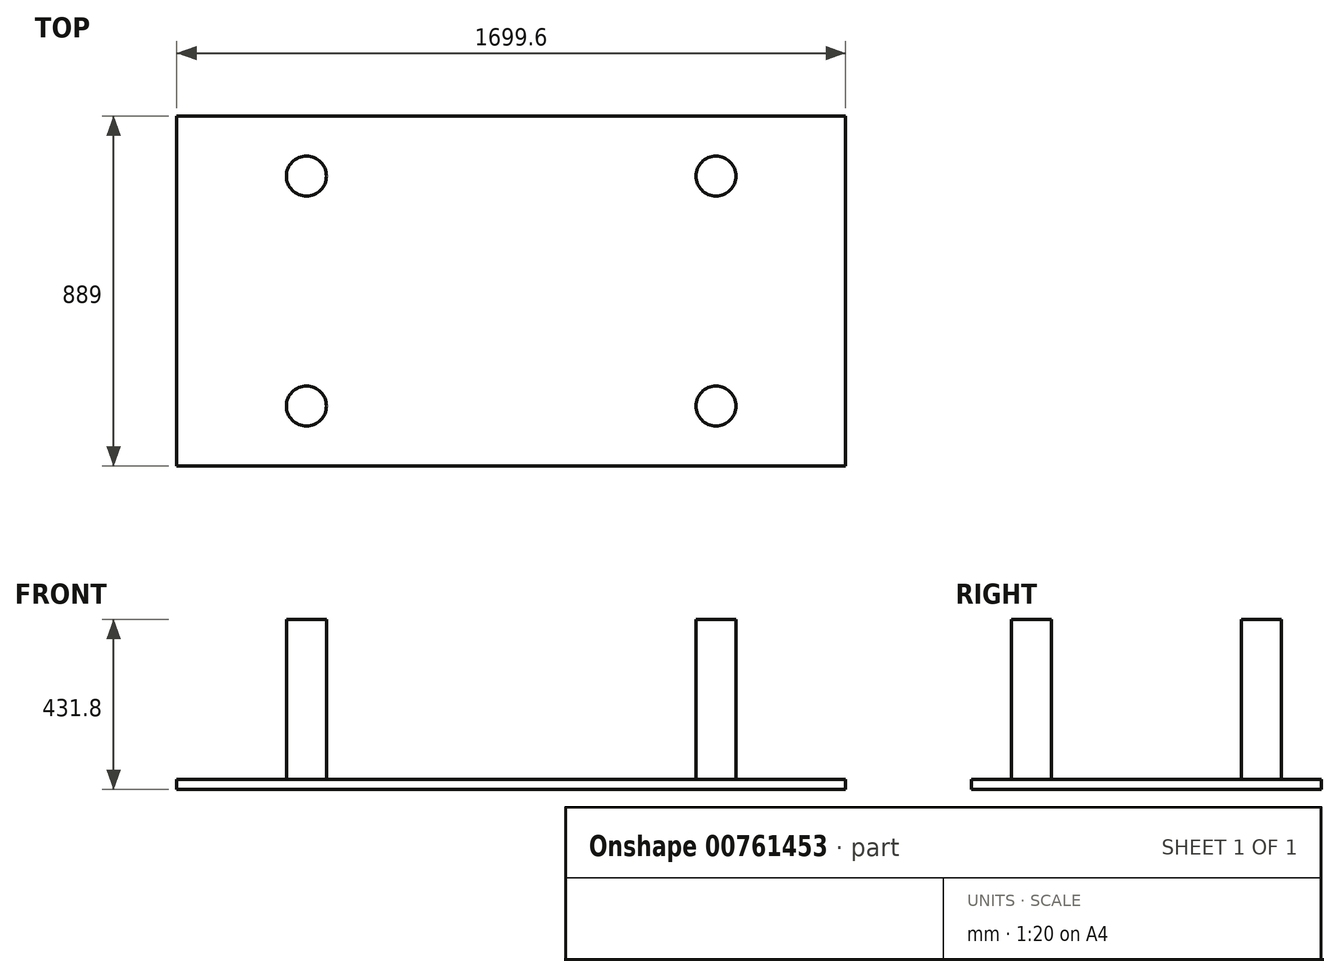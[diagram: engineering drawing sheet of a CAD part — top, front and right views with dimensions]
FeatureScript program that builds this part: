
annotation { "Feature Type Name" : "Feature", "Feature Type Description" : "" }
export const myFeature = defineFeature(function(context is Context, id is Id, definition is map)
    precondition{}
    {
        {
            var Q0;
            Q0=qCreatedBy(makeId("Top.planeOp"),FACE);
            var sketch = newSketch(context, id + "F0", { "sketchPlane" : qUnion([Q0])});
            skLineSegment(sketch, "E0.bottom", {"start": v(-190.5, 381) * mm, "end": v(190.5, 381) * mm});
            skLineSegment(sketch, "E0.top", {"start": v(-190.5, -381) * mm, "end": v(190.5, -381) * mm});
            skLineSegment(sketch, "E0.left", {"start": v(-190.5, 381) * mm, "end": v(-190.5, -381) * mm});
            skLineSegment(sketch, "E0.right", {"start": v(190.5, 381) * mm, "end": v(190.5, -381) * mm});
            skPoint(sketch, "E0.middle", {"position": v(0, 0) * mm});
            skLineSegment(sketch, "E1.bottom", {"start": v(-12.7, 381) * mm, "end": v(12.7, 381) * mm});
            skLineSegment(sketch, "E1.top", {"start": v(-12.7, -381) * mm, "end": v(12.7, -381) * mm});
            skLineSegment(sketch, "E1.left", {"start": v(-12.7, 381) * mm, "end": v(-12.7, -381) * mm});
            skLineSegment(sketch, "E1.right", {"start": v(12.7, 381) * mm, "end": v(12.7, -381) * mm});
            skLineSegment(sketch, "E2", {"start": v(-12.7, 254) * mm, "end": v(12.7, 254) * mm});
            skLineSegment(sketch, "E3", {"start": v(-12.7, 127) * mm, "end": v(12.7, 127) * mm});
            skLineSegment(sketch, "E4", {"start": v(-12.7, 0) * mm, "end": v(12.7, 0) * mm});
            skLineSegment(sketch, "E5", {"start": v(-12.7, -127) * mm, "end": v(12.7, -127) * mm});
            skLineSegment(sketch, "E6", {"start": v(-12.7, -254) * mm, "end": v(12.7, -254) * mm});
            skLineSegment(sketch, "E7.bottom", {"start": v(190.5, 381) * mm, "end": v(-190.5, 381) * mm});
            skLineSegment(sketch, "E7.top", {"start": v(190.5, 508) * mm, "end": v(-190.5, 508) * mm});
            skLineSegment(sketch, "E7.left", {"start": v(190.5, 381) * mm, "end": v(190.5, 508) * mm});
            skLineSegment(sketch, "E7.right", {"start": v(-190.5, 381) * mm, "end": v(-190.5, 508) * mm});
            skLineSegment(sketch, "E8.bottom", {"start": v(849.8, 508) * mm, "end": v(-849.8, 508) * mm});
            skLineSegment(sketch, "E9", {"start": v(-849.8, -381) * mm, "end": v(-190.5, -381) * mm});
            skLineSegment(sketch, "E10", {"start": v(190.5, -381) * mm, "end": v(849.8, -381) * mm});
            skLineSegment(sketch, "E11", {"start": v(849.8, 508) * mm, "end": v(849.8, -381) * mm});
            skLineSegment(sketch, "E12", {"start": v(-849.8, 508) * mm, "end": v(-849.8, -381) * mm});
            skLineSegment(sketch, "E13", {"start": v(-190.5, 508) * mm, "end": v(-849.8, 508) * mm});
            skLineSegment(sketch, "E14", {"start": v(190.5, 508) * mm, "end": v(849.8, 508) * mm});
            skCircle(sketch, "E15", {"center": v(-520.15, 355.6) * mm, "radius": 50.8 * mm});
            skPoint(sketch, "E15.centerSnap0", {"position": v(-520.15, 508) * mm});
            skCircle(sketch, "E16", {"center": v(520.15, 355.6) * mm, "radius": 50.8 * mm});
            skPoint(sketch, "E16.centerSnap0", {"position": v(520.15, 508) * mm});
            skCircle(sketch, "E17", {"center": v(520.15, -228.6) * mm, "radius": 50.8 * mm});
            skCircle(sketch, "E18", {"center": v(-520.15, -228.6) * mm, "radius": 50.8 * mm});
            skSolve(sketch);
        }
        {
            var Q0;
            {var subQ0=sQuery(id+"F0.wireOp",EDGE,"E7.left");Q0=makeQuery(id+"F0.imprint","IMPRINT",FACE,{"disambiguationData":[TD([[makeQuery(id+"F0.imprint","IMPRINT",EDGE,{"derivedFrom":subQ0}),1.0]])]});}
            var Q1;
            {var subQ4=sQuery(id+"F0.wireOp",EDGE,"E0.right");Q1=makeQuery(id+"F0.imprint","IMPRINT",FACE,{"disambiguationData":[TD([[makeQuery(id+"F0.imprint","IMPRINT",EDGE,{"derivedFrom":subQ4}),-1.0]])]});}
            var Q2;
            Q2=makeQuery(id+"F0.imprint","IMPRINT",FACE,{"disambiguationData":[TD([[makeQuery(id+"F0.imprint","IMPRINT",EDGE,{"derivedFrom":sQuery(id+"F0.wireOp",EDGE,"E0.right")}),1.0]])]});
            var Q3;
            Q3=makeQuery(id+"F0.imprint","IMPRINT",FACE,{"disambiguationData":[TD([[makeQuery(id+"F0.imprint","IMPRINT",EDGE,{"derivedFrom":sQuery(id+"F0.wireOp",EDGE,"E16")}),1.0]])]});
            var Q4;
            Q4=makeQuery(id+"F0.imprint","IMPRINT",FACE,{"disambiguationData":[TD([[makeQuery(id+"F0.imprint","IMPRINT",EDGE,{"derivedFrom":sQuery(id+"F0.wireOp",EDGE,"E17")}),1.0]])]});
            var Q5;
            {var subQ4=sQuery(id+"F0.wireOp",EDGE,"E0.left");Q5=makeQuery(id+"F0.imprint","IMPRINT",FACE,{"disambiguationData":[TD([[makeQuery(id+"F0.imprint","IMPRINT",EDGE,{"derivedFrom":subQ4}),1.0]])]});}
            var Q6;
            Q6=makeQuery(id+"F0.imprint","IMPRINT",FACE,{"disambiguationData":[TD([[makeQuery(id+"F0.imprint","IMPRINT",EDGE,{"derivedFrom":sQuery(id+"F0.wireOp",EDGE,"E0.left")}),-1.0]])]});
            var Q7;
            Q7=makeQuery(id+"F0.imprint","IMPRINT",FACE,{"disambiguationData":[TD([[makeQuery(id+"F0.imprint","IMPRINT",EDGE,{"derivedFrom":sQuery(id+"F0.wireOp",EDGE,"E15")}),1.0]])]});
            var Q8;
            Q8=makeQuery(id+"F0.imprint","IMPRINT",FACE,{"disambiguationData":[TD([[makeQuery(id+"F0.imprint","IMPRINT",EDGE,{"derivedFrom":sQuery(id+"F0.wireOp",EDGE,"E18")}),1.0]])]});
            var Q9;
            {var subQ3=sQuery(id+"F0.wireOp",EDGE,"E6");Q9=makeQuery(id+"F0.imprint","IMPRINT",FACE,{"disambiguationData":[TD([[makeQuery(id+"F0.imprint","IMPRINT",EDGE,{"derivedFrom":subQ3}),-1.0]])]});}
            var Q10;
            {var subQ0=sQuery(id+"F0.wireOp",EDGE,"E5");Q10=makeQuery(id+"F0.imprint","IMPRINT",FACE,{"disambiguationData":[TD([[makeQuery(id+"F0.imprint","IMPRINT",EDGE,{"derivedFrom":subQ0}),-1.0]])]});}
            var Q11;
            {var subQ0=sQuery(id+"F0.wireOp",EDGE,"E4");Q11=makeQuery(id+"F0.imprint","IMPRINT",FACE,{"disambiguationData":[TD([[makeQuery(id+"F0.imprint","IMPRINT",EDGE,{"derivedFrom":subQ0}),-1.0]])]});}
            var Q12;
            {var subQ0=sQuery(id+"F0.wireOp",EDGE,"E3");Q12=makeQuery(id+"F0.imprint","IMPRINT",FACE,{"disambiguationData":[TD([[makeQuery(id+"F0.imprint","IMPRINT",EDGE,{"derivedFrom":subQ0}),-1.0]])]});}
            var Q13;
            {var subQ3=sQuery(id+"F0.wireOp",EDGE,"E2");Q13=makeQuery(id+"F0.imprint","IMPRINT",FACE,{"disambiguationData":[TD([[makeQuery(id+"F0.imprint","IMPRINT",EDGE,{"derivedFrom":subQ3}),1.0]])]});}
            var Q14;
            {var subQ0=sQuery(id+"F0.wireOp",EDGE,"E2");Q14=makeQuery(id+"F0.imprint","IMPRINT",FACE,{"disambiguationData":[TD([[makeQuery(id+"F0.imprint","IMPRINT",EDGE,{"derivedFrom":subQ0}),-1.0]])]});}
            extrude(context, id + "F1", {"entities" : qUnion([Q0, Q1, Q2, Q3, Q4, Q5, Q6, Q7, Q8, Q9, Q10, Q11, Q12, Q13, Q14]), "depth" : 25.4 * mm, "offsetDistance" : 25.4 * mm});
        }
        {
            var Q0;
            Q0=makeQuery(id+"F0.imprint","IMPRINT",FACE,{"disambiguationData":[TD([[makeQuery(id+"F0.imprint","IMPRINT",EDGE,{"derivedFrom":sQuery(id+"F0.wireOp",EDGE,"E15")}),1.0]])]});
            var Q1;
            Q1=makeQuery(id+"F0.imprint","IMPRINT",FACE,{"disambiguationData":[TD([[makeQuery(id+"F0.imprint","IMPRINT",EDGE,{"derivedFrom":sQuery(id+"F0.wireOp",EDGE,"E16")}),1.0]])]});
            var Q2;
            Q2=makeQuery(id+"F0.imprint","IMPRINT",FACE,{"disambiguationData":[TD([[makeQuery(id+"F0.imprint","IMPRINT",EDGE,{"derivedFrom":sQuery(id+"F0.wireOp",EDGE,"E17")}),1.0]])]});
            var Q3;
            Q3=makeQuery(id+"F0.imprint","IMPRINT",FACE,{"disambiguationData":[TD([[makeQuery(id+"F0.imprint","IMPRINT",EDGE,{"derivedFrom":sQuery(id+"F0.wireOp",EDGE,"E18")}),1.0]])]});
            extrude(context, id + "F2", {"entities" : qUnion([Q0, Q1, Q2, Q3]), "operationType" : NewBodyOperationType.ADD, "depth" : 431.8 * mm, "offsetDistance" : 25.4 * mm});
        }
    });
